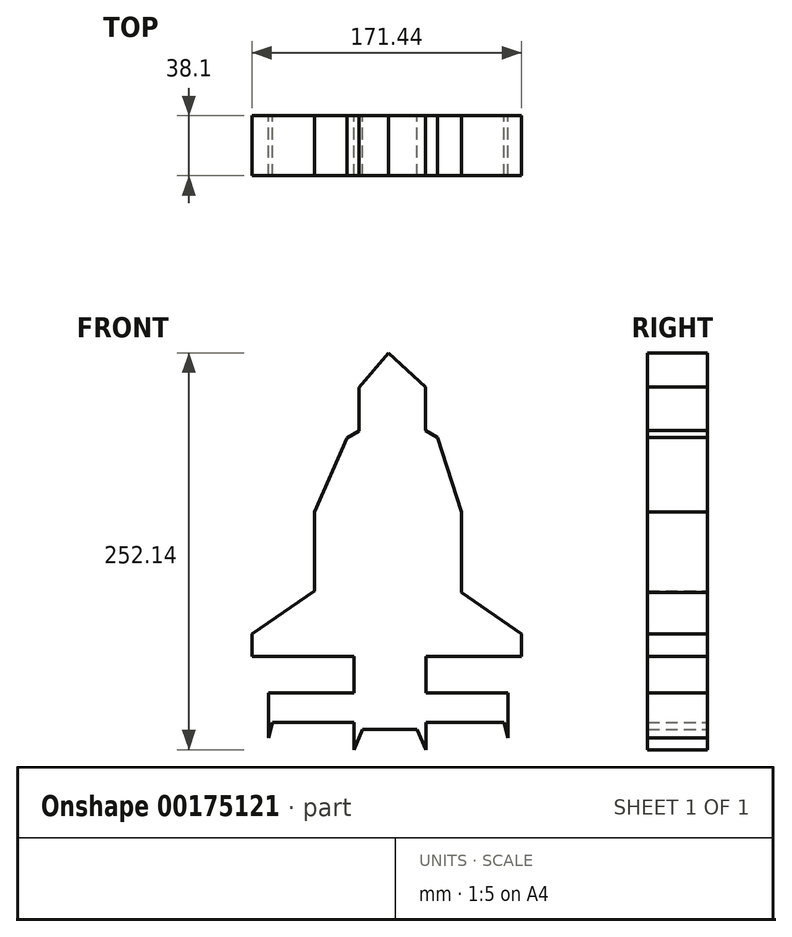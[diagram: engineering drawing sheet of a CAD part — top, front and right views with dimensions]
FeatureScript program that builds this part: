
annotation { "Feature Type Name" : "Feature", "Feature Type Description" : "" }
export const myFeature = defineFeature(function(context is Context, id is Id, definition is map)
    precondition{}
    {
        {
            var Q0;
            Q0=qCreatedBy(makeId("Front.planeOp"),FACE);
            var sketch = newSketch(context, id + "F0", { "sketchPlane" : qUnion([Q0])});
            skLineSegment(sketch, "E0.1", {"start": v(46.36, -26.52) * mm, "end": v(23.96, -66.94) * mm});
            skLineSegment(sketch, "E0.2", {"start": v(23.96, -66.94) * mm, "end": v(-21.86, -67.02) * mm});
            skLineSegment(sketch, "E0.3", {"start": v(-21.86, -67.02) * mm, "end": v(-46.86, -25.42) * mm});
            skPoint(sketch, "E0.0.midPoint", {"position": v(35.02, -6.54) * mm});
            skLineSegment(sketch, "E1", {"start": v(-46.86, -25.42) * mm, "end": v(-46.86, 24.86) * mm});
            skLineSegment(sketch, "E2", {"start": v(46.36, -26.52) * mm, "end": v(46.36, 24.86) * mm});
            skLineSegment(sketch, "E3", {"start": v(-46.86, 24.86) * mm, "end": v(-18.74, 24.86) * mm});
            skLineSegment(sketch, "E4", {"start": v(46.36, 24.86) * mm, "end": v(23.68, 24.86) * mm});
            skArc(sketch, "E5", {"start": v(14, 54.15) * mm, "mid": v(1.72, 57.22) * mm, "end": v(-10.34, 53.36) * mm});
            skPoint(sketch, "E6.orphan", {"position": v(26.16, 45.04) * mm});
            skPoint(sketch, "E7.orphan", {"position": v(23.73, 45.04) * mm});
            skPoint(sketch, "E8.orphan", {"position": v(-18.74, 13.98) * mm});
            skPoint(sketch, "E9.orphan", {"position": v(23.68, 13.43) * mm});
            skPoint(sketch, "E0.cCircle.center.orphan", {"position": v(0, -26.66) * mm});
            skLineSegment(sketch, "E10", {"start": v(-18.74, 24.86) * mm, "end": v(-10.34, 53.36) * mm});
            skLineSegment(sketch, "E11", {"start": v(23.68, 24.86) * mm, "end": v(14, 54.15) * mm});
            skPoint(sketch, "E12.orphan", {"position": v(23.73, 43.22) * mm});
            skLineSegment(sketch, "E13", {"start": v(-21.86, -67.02) * mm, "end": v(-21.86, -113.35) * mm});
            skLineSegment(sketch, "E14", {"start": v(-21.86, -113.35) * mm, "end": v(23.96, -113.35) * mm});
            skLineSegment(sketch, "E15", {"start": v(23.96, -113.35) * mm, "end": v(23.96, -66.94) * mm});
            skPoint(sketch, "E16.endSnap0", {"position": v(-21.86, -90.19) * mm});
            skLineSegment(sketch, "E17", {"start": v(-75.95, -90.19) * mm, "end": v(76.15, -90.19) * mm});
            skLineSegment(sketch, "E18", {"start": v(-75.95, -90.19) * mm, "end": v(-75.95, -108.98) * mm});
            skLineSegment(sketch, "E19", {"start": v(-75.95, -108.98) * mm, "end": v(-21.86, -108.98) * mm});
            skLineSegment(sketch, "E20", {"start": v(76.15, -108.98) * mm, "end": v(76.15, -90.19) * mm});
            skLineSegment(sketch, "E21.trimOffspring", {"start": v(23.96, -108.98) * mm, "end": v(76.15, -108.98) * mm});
            skLineSegment(sketch, "E22", {"start": v(-75.95, -108.98) * mm, "end": v(-75.95, -118.82) * mm});
            skLineSegment(sketch, "E23", {"start": v(-75.95, -118.82) * mm, "end": v(-73.43, -108.98) * mm});
            skLineSegment(sketch, "E24", {"start": v(76.15, -108.98) * mm, "end": v(76.15, -118.82) * mm});
            skLineSegment(sketch, "E25", {"start": v(76.15, -118.82) * mm, "end": v(73.63, -108.98) * mm});
            skLineSegment(sketch, "E26", {"start": v(-21.86, -113.35) * mm, "end": v(-21.86, -126.33) * mm});
            skLineSegment(sketch, "E27", {"start": v(-21.86, -126.33) * mm, "end": v(-16.24, -113.35) * mm});
            skLineSegment(sketch, "E28", {"start": v(23.96, -113.35) * mm, "end": v(23.96, -126.33) * mm});
            skLineSegment(sketch, "E29", {"start": v(23.96, -126.33) * mm, "end": v(18.34, -113.35) * mm});
            skLineSegment(sketch, "E30", {"start": v(-21.86, -67.02) * mm, "end": v(-86.7, -67.14) * mm});
            skLineSegment(sketch, "E31", {"start": v(84.75, -66.94) * mm, "end": v(84.75, -52.77) * mm});
            skLineSegment(sketch, "E32", {"start": v(-86.7, -67.14) * mm, "end": v(-86.7, -67.14) * mm});
            skLineSegment(sketch, "E33", {"start": v(84.75, -52.77) * mm, "end": v(46.36, -26.52) * mm});
            skLineSegment(sketch, "E34", {"start": v(-86.7, -67.14) * mm, "end": v(-86.7, -52.77) * mm});
            skLineSegment(sketch, "E35", {"start": v(-86.7, -52.77) * mm, "end": v(-46.86, -25.42) * mm});
            skLineSegment(sketch, "E36", {"start": v(-18.74, 24.86) * mm, "end": v(-18.74, 103.94) * mm});
            skLineSegment(sketch, "E37", {"start": v(23.68, 24.86) * mm, "end": v(23.68, 104.03) * mm});
            skPoint(sketch, "E38.orphan", {"position": v(46.36, 103.94) * mm});
            skLineSegment(sketch, "E39", {"start": v(0, 76.04) * mm, "end": v(0, 103.94) * mm});
            skLineSegment(sketch, "E40", {"start": v(0, 125.81) * mm, "end": v(-18.74, 103.94) * mm});
            skLineSegment(sketch, "E41", {"start": v(0, 125.81) * mm, "end": v(23.68, 104.03) * mm});
            skLineSegment(sketch, "E42", {"start": v(-18.74, 76.21) * mm, "end": v(-26.23, 71.84) * mm});
            skLineSegment(sketch, "E43", {"start": v(23.68, 76.4) * mm, "end": v(31.35, 71.92) * mm});
            skLineSegment(sketch, "E44", {"start": v(31.35, 71.92) * mm, "end": v(46.36, 24.86) * mm});
            skLineSegment(sketch, "E45", {"start": v(-26.23, 71.84) * mm, "end": v(-46.86, 24.86) * mm});
            skPoint(sketch, "E46.start.orphan", {"position": v(27.43, -66.94) * mm});
            skLineSegment(sketch, "E47", {"start": v(23.96, -66.94) * mm, "end": v(84.75, -66.94) * mm});
            skSolve(sketch);
        }
        {
            var Q0;
            {var subQ4=sQuery(id+"F0.wireOp",EDGE,"E20");Q0=makeQuery(id+"F0.imprint","IMPRINT",FACE,{"disambiguationData":[TD([[makeQuery(id+"F0.imprint","IMPRINT",EDGE,{"derivedFrom":subQ4}),1.0]])]});}
            var Q1;
            {var subQ0=sQuery(id+"F0.wireOp",EDGE,"E3");Q1=makeQuery(id+"F0.imprint","IMPRINT",FACE,{"disambiguationData":[TD([[makeQuery(id+"F0.imprint","IMPRINT",EDGE,{"derivedFrom":subQ0}),1.0]])]});}
            var Q2;
            {var subQ1=sQuery(id+"F0.wireOp",EDGE,"E18");Q2=makeQuery(id+"F0.imprint","IMPRINT",FACE,{"disambiguationData":[TD([[makeQuery(id+"F0.imprint","IMPRINT",EDGE,{"derivedFrom":subQ1}),1.0]])]});}
            var Q3;
            {var subQ0=sQuery(id+"F0.wireOp",EDGE,"E4");Q3=makeQuery(id+"F0.imprint","IMPRINT",FACE,{"disambiguationData":[TD([[makeQuery(id+"F0.imprint","IMPRINT",EDGE,{"derivedFrom":subQ0}),-1.0]])]});}
            var Q4;
            {var subQ3=sQuery(id+"F0.wireOp",EDGE,"E13");var subQ9=makeQuery(id+"F0.imprint","INTERSECT",VERTEX,{"derivedFrom":[subQ3,sQuery(id+"F0.wireOp",EDGE,"E19")]});Q4=makeQuery(id+"F0.imprint","IMPRINT",FACE,{"disambiguationData":[TD([[makeQuery(id+"F0.imprint","IMPRINT",EDGE,{"disambiguationData":[TD([[subQ9,1.0]])],"derivedFrom":subQ3}),1.0]])]});}
            var Q5;
            Q5=makeQuery(id+"F0.imprint","IMPRINT",FACE,{"disambiguationData":[TD([[makeQuery(id+"F0.imprint","IMPRINT",EDGE,{"derivedFrom":sQuery(id+"F0.wireOp",EDGE,"E0.1")}),1.0]])]});
            var Q6;
            {var subQ0=sQuery(id+"F0.wireOp",EDGE,"E0.2");Q6=makeQuery(id+"F0.imprint","IMPRINT",FACE,{"disambiguationData":[TD([[makeQuery(id+"F0.imprint","IMPRINT",EDGE,{"derivedFrom":subQ0}),1.0]])]});}
            var Q7;
            Q7=makeQuery(id+"F0.imprint","IMPRINT",FACE,{"disambiguationData":[TD([[makeQuery(id+"F0.imprint","IMPRINT",EDGE,{"derivedFrom":sQuery(id+"F0.wireOp",EDGE,"E0.1")}),-1.0]])]});
            var Q8;
            Q8=makeQuery(id+"F0.imprint","IMPRINT",FACE,{"disambiguationData":[TD([[makeQuery(id+"F0.imprint","IMPRINT",EDGE,{"derivedFrom":sQuery(id+"F0.wireOp",EDGE,"E0.3")}),1.0]])]});
            var Q9;
            Q9=makeQuery(id+"F0.imprint","IMPRINT",FACE,{"disambiguationData":[TD([[makeQuery(id+"F0.imprint","IMPRINT",EDGE,{"derivedFrom":sQuery(id+"F0.wireOp",EDGE,"E5")}),-1.0]])]});
            var Q10;
            {var subQ0=sQuery(id+"F0.wireOp",EDGE,"E24");Q10=makeQuery(id+"F0.imprint","IMPRINT",FACE,{"disambiguationData":[TD([[makeQuery(id+"F0.imprint","IMPRINT",EDGE,{"derivedFrom":subQ0}),-1.0]])]});}
            var Q11;
            {var subQ0=sQuery(id+"F0.wireOp",EDGE,"E22");Q11=makeQuery(id+"F0.imprint","IMPRINT",FACE,{"disambiguationData":[TD([[makeQuery(id+"F0.imprint","IMPRINT",EDGE,{"derivedFrom":subQ0}),1.0]])]});}
            var Q12;
            {var subQ0=sQuery(id+"F0.wireOp",EDGE,"E28");Q12=makeQuery(id+"F0.imprint","IMPRINT",FACE,{"disambiguationData":[TD([[makeQuery(id+"F0.imprint","IMPRINT",EDGE,{"derivedFrom":subQ0}),-1.0]])]});}
            var Q13;
            {var subQ0=sQuery(id+"F0.wireOp",EDGE,"E26");Q13=makeQuery(id+"F0.imprint","IMPRINT",FACE,{"disambiguationData":[TD([[makeQuery(id+"F0.imprint","IMPRINT",EDGE,{"derivedFrom":subQ0}),1.0]])]});}
            extrude(context, id + "F1", {"entities" : qUnion([Q0, Q1, Q2, Q3, Q4, Q5, Q6, Q7, Q8, Q9, Q10, Q11, Q12, Q13]), "endBound" : BoundingType.SYMMETRIC, "depth" : 25.4 * mm});
        }
        {
            var Q0;
            Q0=makeQuery(id+"F1.opExtrude","CAP_FACE",FACE,{"disambiguationData":[OSD([sQuery(id+"F0.wireOp",EDGE,"E1"),sQuery(id+"F0.wireOp",EDGE,"E2"),sQuery(id+"F0.wireOp",EDGE,"E13"),sQuery(id+"F0.wireOp",EDGE,"E14"),sQuery(id+"F0.wireOp",EDGE,"E15"),sQuery(id+"F0.wireOp",EDGE,"E17"),sQuery(id+"F0.wireOp",EDGE,"E18"),sQuery(id+"F0.wireOp",EDGE,"E19"),sQuery(id+"F0.wireOp",EDGE,"E20"),sQuery(id+"F0.wireOp",EDGE,"E21.trimOffspring"),sQuery(id+"F0.wireOp",EDGE,"E22"),sQuery(id+"F0.wireOp",EDGE,"E23"),sQuery(id+"F0.wireOp",EDGE,"E24"),sQuery(id+"F0.wireOp",EDGE,"E25"),sQuery(id+"F0.wireOp",EDGE,"E26"),sQuery(id+"F0.wireOp",EDGE,"E27"),sQuery(id+"F0.wireOp",EDGE,"E28"),sQuery(id+"F0.wireOp",EDGE,"E29"),sQuery(id+"F0.wireOp",EDGE,"E30"),sQuery(id+"F0.wireOp",EDGE,"E31"),sQuery(id+"F0.wireOp",EDGE,"E33"),sQuery(id+"F0.wireOp",EDGE,"E34"),sQuery(id+"F0.wireOp",EDGE,"E35"),sQuery(id+"F0.wireOp",EDGE,"E36"),sQuery(id+"F0.wireOp",EDGE,"E37"),sQuery(id+"F0.wireOp",EDGE,"E40"),sQuery(id+"F0.wireOp",EDGE,"E41"),sQuery(id+"F0.wireOp",EDGE,"E42"),sQuery(id+"F0.wireOp",EDGE,"E43"),sQuery(id+"F0.wireOp",EDGE,"E44"),sQuery(id+"F0.wireOp",EDGE,"E45"),sQuery(id+"F0.wireOp",EDGE,"E47")])],"isStart":true});
            var sketch = newSketch(context, id + "F2", { "sketchPlane" : qUnion([Q0])});
            skCircle(sketch, "E48", {"center": v(0, 77.13) * mm, "radius": 16.87 * mm});
            skSolve(sketch);
        }
        {
            var Q0;
            Q0 = qSketchRegion(id + "F0", true);
            extrude(context, id + "F3", {"entities" : qUnion([Q0]), "operationType" : NewBodyOperationType.ADD, "depth" : 25.4 * mm});
        }
    });
